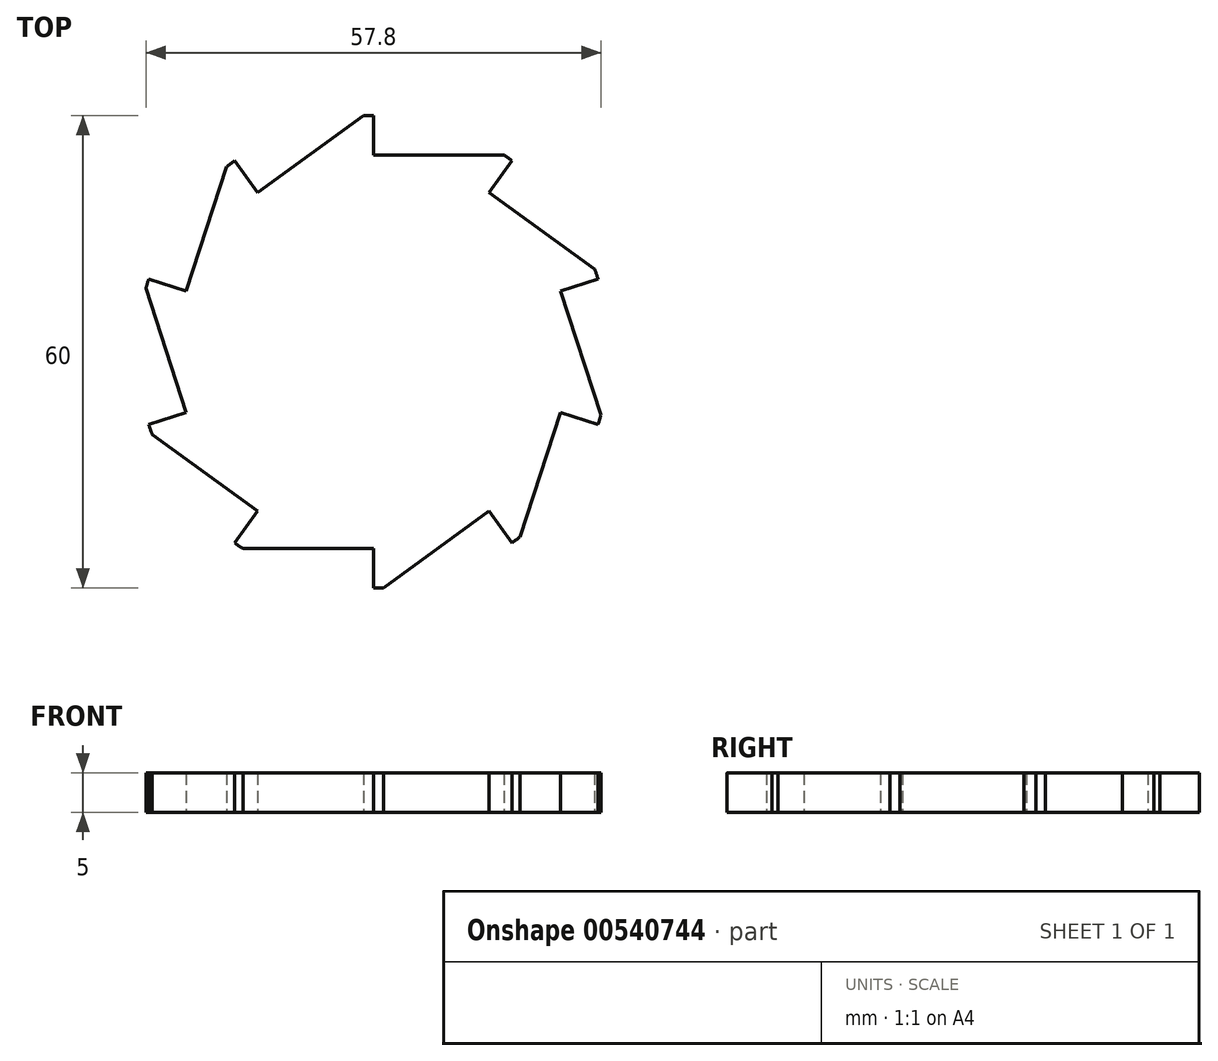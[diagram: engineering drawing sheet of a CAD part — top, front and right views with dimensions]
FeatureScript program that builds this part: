
annotation { "Feature Type Name" : "Feature", "Feature Type Description" : "" }
export const myFeature = defineFeature(function(context is Context, id is Id, definition is map)
    precondition{}
    {
        {
            var Q0;
            Q0=qCreatedBy(makeId("Top.planeOp"),FACE);
            var sketch = newSketch(context, id + "F0", { "sketchPlane" : qUnion([Q0])});
            skCircle(sketch, "E0", {"center": v(0, 0) * mm, "radius": 30 * mm});
            skLineSegment(sketch, "E1", {"start": v(0, 30) * mm, "end": v(0, 25) * mm});
            skLineSegment(sketch, "E2", {"start": v(0, 25) * mm, "end": v(16.58, 25) * mm});
            skLineSegment(sketch, "E3.1.0", {"start": v(-14.7, 20.23) * mm, "end": v(-1.28, 29.97) * mm});
            skLineSegment(sketch, "E3.1.1", {"start": v(-17.63, 24.27) * mm, "end": v(-14.7, 20.23) * mm});
            skLineSegment(sketch, "E3.2.0", {"start": v(-23.78, 7.73) * mm, "end": v(-18.65, 23.5) * mm});
            skLineSegment(sketch, "E3.2.1", {"start": v(-28.53, 9.27) * mm, "end": v(-23.78, 7.73) * mm});
            skLineSegment(sketch, "E3.3.0", {"start": v(-23.78, -7.73) * mm, "end": v(-28.9, 8.05) * mm});
            skLineSegment(sketch, "E3.3.1", {"start": v(-28.53, -9.27) * mm, "end": v(-23.78, -7.73) * mm});
            skLineSegment(sketch, "E3.4.0", {"start": v(-14.7, -20.23) * mm, "end": v(-28.11, -10.48) * mm});
            skLineSegment(sketch, "E3.4.1", {"start": v(-17.63, -24.27) * mm, "end": v(-14.7, -20.23) * mm});
            skLineSegment(sketch, "E3.5.0", {"start": v(0, -25) * mm, "end": v(-16.58, -25) * mm});
            skLineSegment(sketch, "E3.5.1", {"start": v(0, -30) * mm, "end": v(0, -25) * mm});
            skLineSegment(sketch, "E3.6.0", {"start": v(14.7, -20.23) * mm, "end": v(1.28, -29.97) * mm});
            skLineSegment(sketch, "E3.6.1", {"start": v(17.63, -24.27) * mm, "end": v(14.7, -20.23) * mm});
            skLineSegment(sketch, "E3.7.0", {"start": v(23.78, -7.73) * mm, "end": v(18.65, -23.5) * mm});
            skLineSegment(sketch, "E3.7.1", {"start": v(28.53, -9.27) * mm, "end": v(23.78, -7.73) * mm});
            skLineSegment(sketch, "E3.8.0", {"start": v(23.78, 7.73) * mm, "end": v(28.9, -8.05) * mm});
            skLineSegment(sketch, "E3.8.1", {"start": v(28.53, 9.27) * mm, "end": v(23.78, 7.73) * mm});
            skLineSegment(sketch, "E3.9.0", {"start": v(14.7, 20.23) * mm, "end": v(28.11, 10.48) * mm});
            skLineSegment(sketch, "E3.9.1", {"start": v(17.63, 24.27) * mm, "end": v(14.7, 20.23) * mm});
            skSolve(sketch);
        }
        {
            var Q0;
            {var subQ14=sQuery(id+"F0.wireOp",EDGE,"E1");Q0=makeQuery(id+"F0.imprint","IMPRINT",FACE,{"disambiguationData":[TD([[makeQuery(id+"F0.imprint","IMPRINT",EDGE,{"derivedFrom":subQ14}),-1.0]])]});}
            extrude(context, id + "F1", {"entities" : qUnion([Q0]), "depth" : 5 * mm, "offsetDistance" : 25 * mm});
        }
    });
